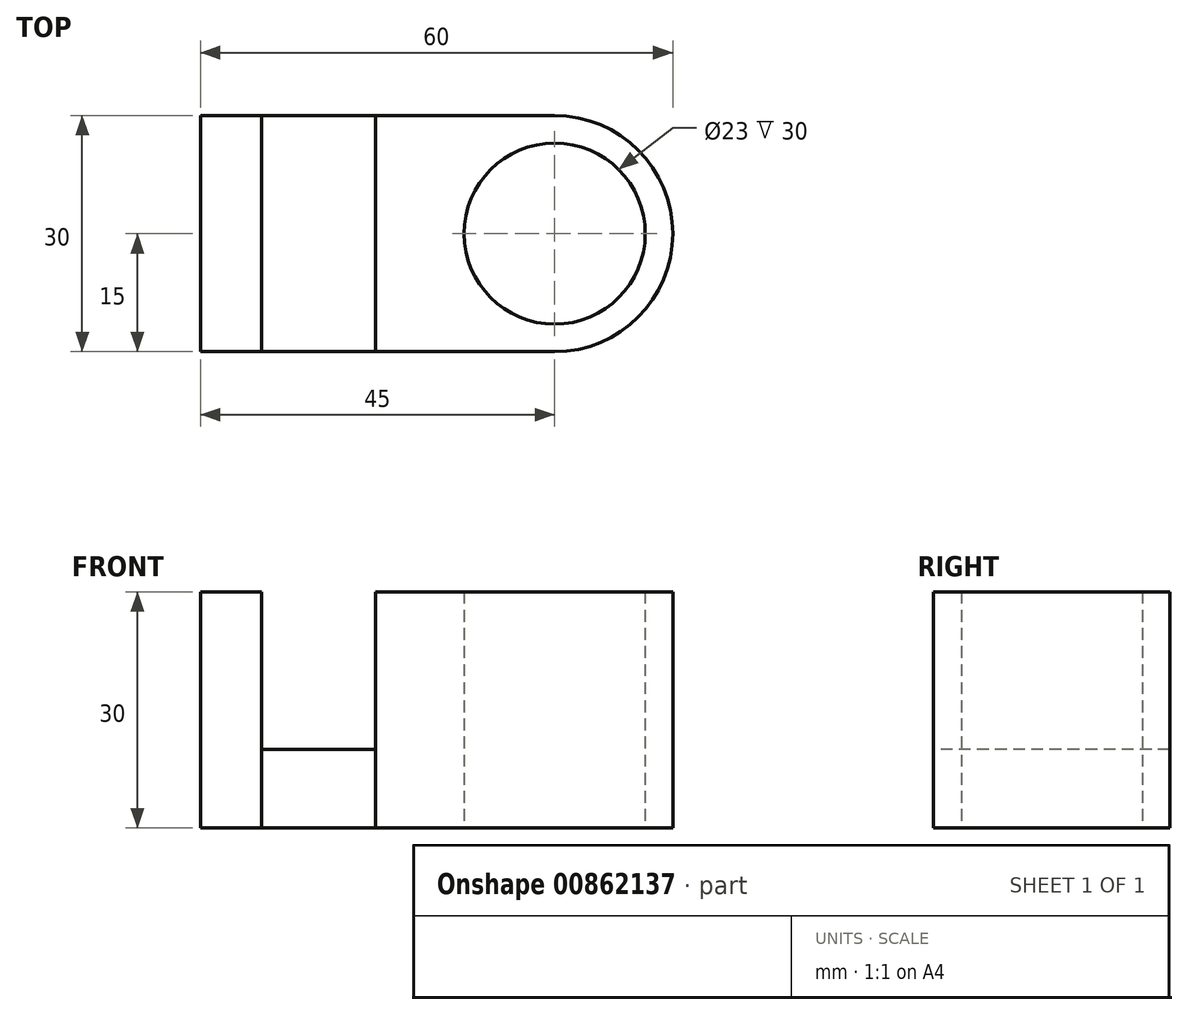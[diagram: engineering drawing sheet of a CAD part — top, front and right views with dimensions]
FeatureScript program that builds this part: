
annotation { "Feature Type Name" : "Feature", "Feature Type Description" : "" }
export const myFeature = defineFeature(function(context is Context, id is Id, definition is map)
    precondition{}
    {
        {
            var Q0;
            Q0=qCreatedBy(makeId("Top.planeOp"),FACE);
            var sketch = newSketch(context, id + "F0", { "sketchPlane" : qUnion([Q0])});
            skLineSegment(sketch, "E0.bottom", {"start": v(30, -15) * mm, "end": v(-30, -15) * mm});
            skLineSegment(sketch, "E0.top", {"start": v(30, 15) * mm, "end": v(-30, 15) * mm});
            skLineSegment(sketch, "E0.left", {"start": v(30, -15) * mm, "end": v(30, 15) * mm});
            skLineSegment(sketch, "E0.right", {"start": v(-30, -15) * mm, "end": v(-30, 15) * mm});
            skPoint(sketch, "E0.middle", {"position": v(0, 0) * mm});
            skLineSegment(sketch, "E1", {"start": v(0, 15) * mm, "end": v(0, -15) * mm});
            skLineSegment(sketch, "E2", {"start": v(-22.25, 15) * mm, "end": v(-22.25, -15) * mm});
            skLineSegment(sketch, "E3.MirrorCS", {"start": v(-7.75, 15) * mm, "end": v(-7.75, -15) * mm});
            skLineSegment(sketch, "E4", {"start": v(30, -28.15) * mm, "end": v(0, -28.15) * mm});
            skCircle(sketch, "E5", {"center": v(15, 0) * mm, "radius": 11.5 * mm});
            skPoint(sketch, "E5.centerSnap0", {"position": v(30, 0) * mm});
            skPoint(sketch, "E5.centerSnap1", {"position": v(15, -28.15) * mm});
            skSolve(sketch);
        }
        {
            var Q0;
            {var subQ0=sQuery(id+"F0.wireOp",EDGE,"E0.left");Q0=makeQuery(id+"F0.imprint","IMPRINT",FACE,{"disambiguationData":[TD([[makeQuery(id+"F0.imprint","IMPRINT",EDGE,{"derivedFrom":subQ0}),1.0]])]});}
            extrude(context, id + "F1", {"entities" : qUnion([Q0]), "depth" : 30 * mm, "offsetDistance" : 25 * mm});
        }
        {
            var Q0;
            {var subQ0=sQuery(id+"F0.wireOp",EDGE,"E0.right");Q0=makeQuery(id+"F0.imprint","IMPRINT",FACE,{"disambiguationData":[TD([[makeQuery(id+"F0.imprint","IMPRINT",EDGE,{"derivedFrom":subQ0}),-1.0]])]});}
            var Q1;
            {var subQ0=sQuery(id+"F0.wireOp",EDGE,"E1");Q1=makeQuery(id+"F0.imprint","IMPRINT",FACE,{"disambiguationData":[TD([[makeQuery(id+"F0.imprint","IMPRINT",EDGE,{"derivedFrom":subQ0}),-1.0]])]});}
            extrude(context, id + "F2", {"entities" : qUnion([Q0, Q1]), "operationType" : NewBodyOperationType.ADD, "depth" : 30 * mm, "offsetDistance" : 25 * mm});
        }
        {
            var Q0;
            {var subQ0=sQuery(id+"F0.wireOp",EDGE,"E2");Q0=makeQuery(id+"F0.imprint","IMPRINT",FACE,{"disambiguationData":[TD([[makeQuery(id+"F0.imprint","IMPRINT",EDGE,{"derivedFrom":subQ0}),1.0]])]});}
            extrude(context, id + "F3", {"entities" : qUnion([Q0]), "depth" : 10 * mm, "offsetDistance" : 25 * mm});
        }
        {
            var Q0;
            Q0=makeQuery(id+"F1.opExtrude","SWEPT_EDGE",EDGE,{"disambiguationData":[OSD([sQuery(id+"F0.wireOp",EDGE,"E0.bottom"),sQuery(id+"F0.wireOp",EDGE,"E0.left")])]});
            var Q1;
            Q1=makeQuery(id+"F1.opExtrude","SWEPT_EDGE",EDGE,{"disambiguationData":[OSD([sQuery(id+"F0.wireOp",EDGE,"E0.top"),sQuery(id+"F0.wireOp",EDGE,"E0.left")])]});
            fillet(context, id + "F4", {"entities" : qUnion([Q0, Q1]), "radius" : 15 * mm, "tangentPropagation" : true, "allowEdgeOverflow" : false});
        }
    });
